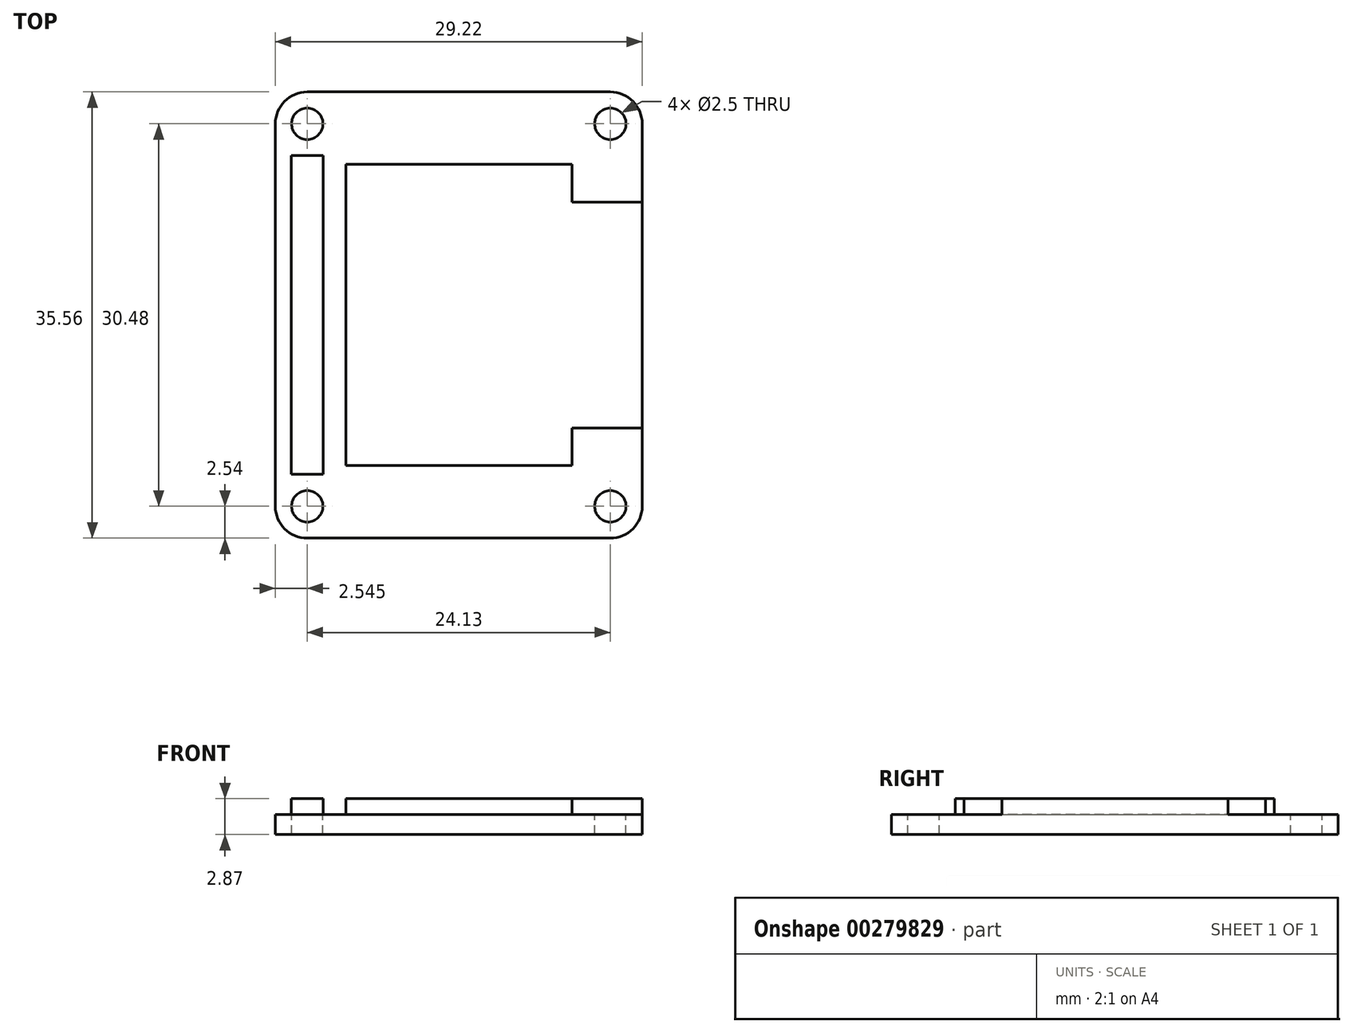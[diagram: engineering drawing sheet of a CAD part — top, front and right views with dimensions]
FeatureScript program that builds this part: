
annotation { "Feature Type Name" : "Feature", "Feature Type Description" : "" }
export const myFeature = defineFeature(function(context is Context, id is Id, definition is map)
    precondition{}
    {
        {
            var Q0;
            Q0=qCreatedBy(makeId("Top.planeOp"),FACE);
            var sketch = newSketch(context, id + "F0", { "sketchPlane" : qUnion([Q0])});
            skLineSegment(sketch, "E0.bottom", {"start": v(-12.06, 17.78) * mm, "end": v(12.07, 17.78) * mm});
            skLineSegment(sketch, "E0.top", {"start": v(-12.07, -17.78) * mm, "end": v(12.06, -17.78) * mm});
            skLineSegment(sketch, "E0.left", {"start": v(-14.6, 15.24) * mm, "end": v(-14.6, -15.24) * mm});
            skLineSegment(sketch, "E0.right", {"start": v(14.6, 15.24) * mm, "end": v(14.6, -15.24) * mm});
            skPoint(sketch, "E0.middle", {"position": v(0, 0) * mm});
            skPoint(sketch, "E1.visualSharp", {"position": v(-14.6, 17.78) * mm});
            skArc(sketch, "E1.filletArc", {"start": v(-12.06, 17.78) * mm, "mid": v(-13.86, 17.04) * mm, "end": v(-14.6, 15.24) * mm});
            skPoint(sketch, "E2.visualSharp", {"position": v(14.6, 17.78) * mm});
            skArc(sketch, "E2.filletArc", {"start": v(14.6, 15.24) * mm, "mid": v(13.86, 17.04) * mm, "end": v(12.07, 17.78) * mm});
            skPoint(sketch, "E3.visualSharp", {"position": v(14.6, -17.78) * mm});
            skArc(sketch, "E3.filletArc", {"start": v(12.06, -17.78) * mm, "mid": v(13.86, -17.04) * mm, "end": v(14.6, -15.24) * mm});
            skPoint(sketch, "E4.visualSharp", {"position": v(-14.6, -17.78) * mm});
            skArc(sketch, "E4.filletArc", {"start": v(-14.6, -15.24) * mm, "mid": v(-13.86, -17.04) * mm, "end": v(-12.07, -17.78) * mm});
            skCircle(sketch, "E5", {"center": v(-12.06, -15.24) * mm, "radius": 1.25 * mm});
            skCircle(sketch, "E6", {"center": v(-12.06, 15.24) * mm, "radius": 1.25 * mm});
            skCircle(sketch, "E7", {"center": v(12.06, 15.24) * mm, "radius": 1.25 * mm});
            skCircle(sketch, "E8", {"center": v(12.06, -15.24) * mm, "radius": 1.25 * mm});
            skSolve(sketch);
        }
        {
            var Q0;
            Q0=makeQuery(id+"F0.imprint","IMPRINT",FACE,{"disambiguationData":[TD([[makeQuery(id+"F0.imprint","IMPRINT",EDGE,{"derivedFrom":sQuery(id+"F0.wireOp",EDGE,"E0.bottom")}),-1.0]])]});
            extrude(context, id + "F1", {"entities" : qUnion([Q0]), "oppositeDirection" : true, "depth" : 1.6 * mm});
        }
        {
            var Q0;
            Q0=qCreatedBy(makeId("Top.planeOp"),FACE);
            var sketch = newSketch(context, id + "F2", { "sketchPlane" : qUnion([Q0])});
            skLineSegment(sketch, "E9.bottom", {"start": v(-10.8, -12.7) * mm, "end": v(-13.34, -12.7) * mm});
            skLineSegment(sketch, "E9.top", {"start": v(-10.8, 12.7) * mm, "end": v(-13.33, 12.7) * mm});
            skLineSegment(sketch, "E9.left", {"start": v(-10.8, -12.7) * mm, "end": v(-10.8, 12.7) * mm});
            skLineSegment(sketch, "E9.right", {"start": v(-13.34, -12.7) * mm, "end": v(-13.33, 12.7) * mm});
            skPoint(sketch, "E9.middle", {"position": v(-12.07, 0) * mm});
            skSolve(sketch);
        }
        {
            var Q0;
            Q0 = qSketchRegion(id + "F2", true);
            extrude(context, id + "F3", {"entities" : qUnion([Q0]), "operationType" : NewBodyOperationType.ADD, "depth" : 1.27 * mm});
        }
        {
            var Q0;
            Q0=makeQuery(id+"F1.opExtrude","CAP_FACE",FACE,{"disambiguationData":[OSD([sQuery(id+"F0.wireOp",EDGE,"E0.bottom"),sQuery(id+"F0.wireOp",EDGE,"E0.top"),sQuery(id+"F0.wireOp",EDGE,"E0.left"),sQuery(id+"F0.wireOp",EDGE,"E0.right"),sQuery(id+"F0.wireOp",EDGE,"E1.filletArc"),sQuery(id+"F0.wireOp",EDGE,"E2.filletArc"),sQuery(id+"F0.wireOp",EDGE,"E3.filletArc"),sQuery(id+"F0.wireOp",EDGE,"E4.filletArc"),sQuery(id+"F0.wireOp",EDGE,"E5"),sQuery(id+"F0.wireOp",EDGE,"E6"),sQuery(id+"F0.wireOp",EDGE,"E7"),sQuery(id+"F0.wireOp",EDGE,"E8")])],"isStart":true});
            var sketch = newSketch(context, id + "F4", { "sketchPlane" : qUnion([Q0])});
            skLineSegment(sketch, "E10.bottom", {"start": v(9, -12) * mm, "end": v(-9, -12) * mm});
            skLineSegment(sketch, "E10.top", {"start": v(9, 12) * mm, "end": v(-9, 12) * mm});
            skLineSegment(sketch, "E10.left", {"start": v(9, -12) * mm, "end": v(9, 12) * mm});
            skLineSegment(sketch, "E10.right", {"start": v(-9, -12) * mm, "end": v(-9, 12) * mm});
            skPoint(sketch, "E10.middle", {"position": v(0, 0) * mm});
            skLineSegment(sketch, "E11.bottom", {"start": v(9, 9) * mm, "end": v(14.6, 9) * mm});
            skLineSegment(sketch, "E11.top", {"start": v(9, -9) * mm, "end": v(14.6, -9) * mm});
            skLineSegment(sketch, "E11.left", {"start": v(9, 9) * mm, "end": v(9, -9) * mm});
            skLineSegment(sketch, "E11.right", {"start": v(14.6, 9) * mm, "end": v(14.6, -9) * mm});
            skSolve(sketch);
        }
        {
            var Q0;
            Q0 = qSketchRegion(id + "F4", true);
            extrude(context, id + "F5", {"entities" : qUnion([Q0]), "operationType" : NewBodyOperationType.ADD, "depth" : 1.27 * mm});
        }
    });
